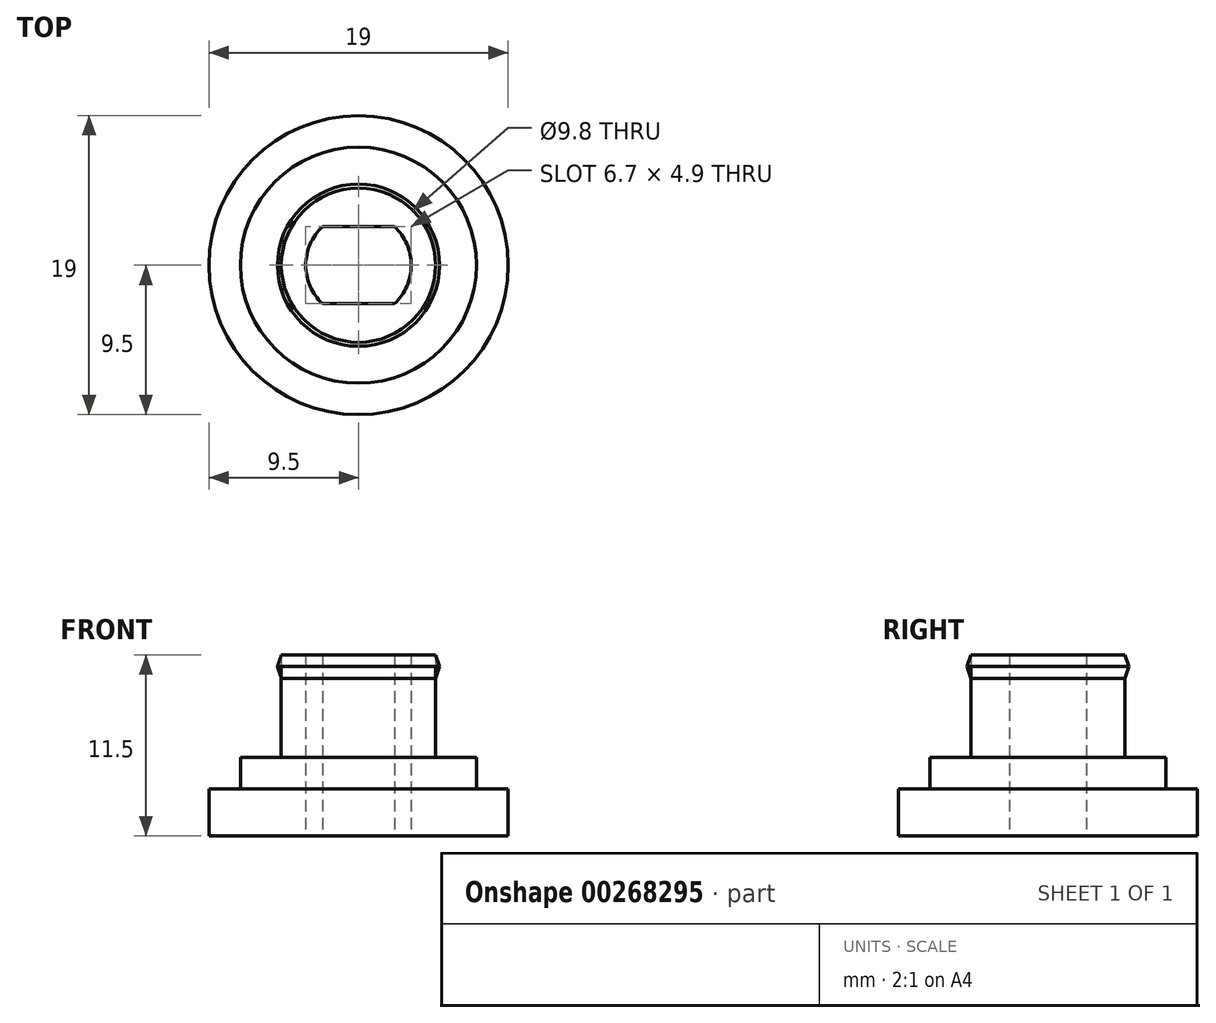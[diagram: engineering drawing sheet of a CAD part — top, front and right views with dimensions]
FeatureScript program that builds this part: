
annotation { "Feature Type Name" : "Feature", "Feature Type Description" : "" }
export const myFeature = defineFeature(function(context is Context, id is Id, definition is map)
    precondition{}
    {
        {
            var Q0;
            Q0=qCreatedBy(makeId("Top.planeOp"),FACE);
            var sketch = newSketch(context, id + "F0", { "sketchPlane" : qUnion([Q0])});
            skCircle(sketch, "E0", {"center": v(0, 0) * mm, "radius": 9.5 * mm});
            skCircle(sketch, "E1", {"center": v(0, 0) * mm, "radius": 7.5 * mm});
            skCircle(sketch, "E2", {"center": v(0, 0) * mm, "radius": 4.9 * mm});
            skArc(sketch, "E3", {"start": v(-2.28, 2.45) * mm, "mid": v(-3.35, 0) * mm, "end": v(-2.28, -2.45) * mm});
            skLineSegment(sketch, "E4.bottom", {"start": v(2.28, -2.45) * mm, "end": v(-2.28, -2.45) * mm});
            skLineSegment(sketch, "E4.top", {"start": v(2.28, 2.45) * mm, "end": v(-2.28, 2.45) * mm});
            skArc(sketch, "E5.trimOffspring", {"start": v(2.28, -2.45) * mm, "mid": v(3.35, 0) * mm, "end": v(2.28, 2.45) * mm});
            skSolve(sketch);
        }
        {
            var Q0;
            Q0=qSketchRegion(id+"F0",true);
            extrude(context, id + "F1", {"entities" : qUnion([Q0]), "depth" : 3 * mm});
        }
        {
            var Q0;
            Q0=makeQuery(id+"F0.imprint","IMPRINT",FACE,{"disambiguationData":[TD([[makeQuery(id+"F0.imprint","IMPRINT",EDGE,{"derivedFrom":sQuery(id+"F0.wireOp",EDGE,"E1")}),1.0]])]});
            extrude(context, id + "F2", {"entities" : qUnion([Q0]), "operationType" : NewBodyOperationType.ADD, "depth" : 5 * mm});
        }
        {
            var Q0;
            Q0=makeQuery(id+"F0.imprint","IMPRINT",FACE,{"disambiguationData":[TD([[makeQuery(id+"F0.imprint","IMPRINT",EDGE,{"derivedFrom":sQuery(id+"F0.wireOp",EDGE,"E2")}),1.0]])]});
            extrude(context, id + "F3", {"entities" : qUnion([Q0]), "operationType" : NewBodyOperationType.ADD, "depth" : 11.5 * mm});
        }
        {
            var Q0;
            Q0=qCreatedBy(makeId("Front.planeOp"),FACE);
            var sketch = newSketch(context, id + "F4", { "sketchPlane" : qUnion([Q0])});
            skLineSegment(sketch, "E6.bottom", {"start": v(4.9, 11.5) * mm, "end": v(5.15, 11.5) * mm, "construction": true});
            skLineSegment(sketch, "E6.top", {"start": v(4.9, 10) * mm, "end": v(5.15, 10) * mm, "construction": true});
            skLineSegment(sketch, "E6.left", {"start": v(4.9, 11.5) * mm, "end": v(4.9, 10) * mm, "construction": true});
            skLineSegment(sketch, "E6.right", {"start": v(5.15, 11.5) * mm, "end": v(5.15, 10) * mm, "construction": true});
            skPoint(sketch, "E7", {"position": v(5.15, 10.75) * mm});
            skLineSegment(sketch, "E8", {"start": v(4.9, 11.5) * mm, "end": v(5.15, 10.75) * mm});
            skLineSegment(sketch, "E9", {"start": v(5.15, 10.75) * mm, "end": v(4.9, 10) * mm});
            skLineSegment(sketch, "E10", {"start": v(4.9, 11.5) * mm, "end": v(4.9, 10) * mm});
            skLineSegment(sketch, "E11", {"start": v(4.9, 11.5) * mm, "end": v(4.9, 5) * mm});
            skLineSegment(sketch, "E12", {"start": v(-4.9, 5) * mm, "end": v(-4.9, 11.5) * mm});
            skLineSegment(sketch, "E13", {"start": v(0, 0) * mm, "end": v(0, 17.95) * mm});
            skSolve(sketch);
        }
        {
            var Q0;
            Q0=qSketchRegion(id+"F4",true);
            var Q1;
            Q1=sQuery(id+"F4.wireOp",EDGE,"E13");
            revolve(context, id + "F5", {"entities" : qUnion([Q0]), "axis" : qUnion([Q1]), "revolveType" : RevolveType.FULL});
        }
    });
